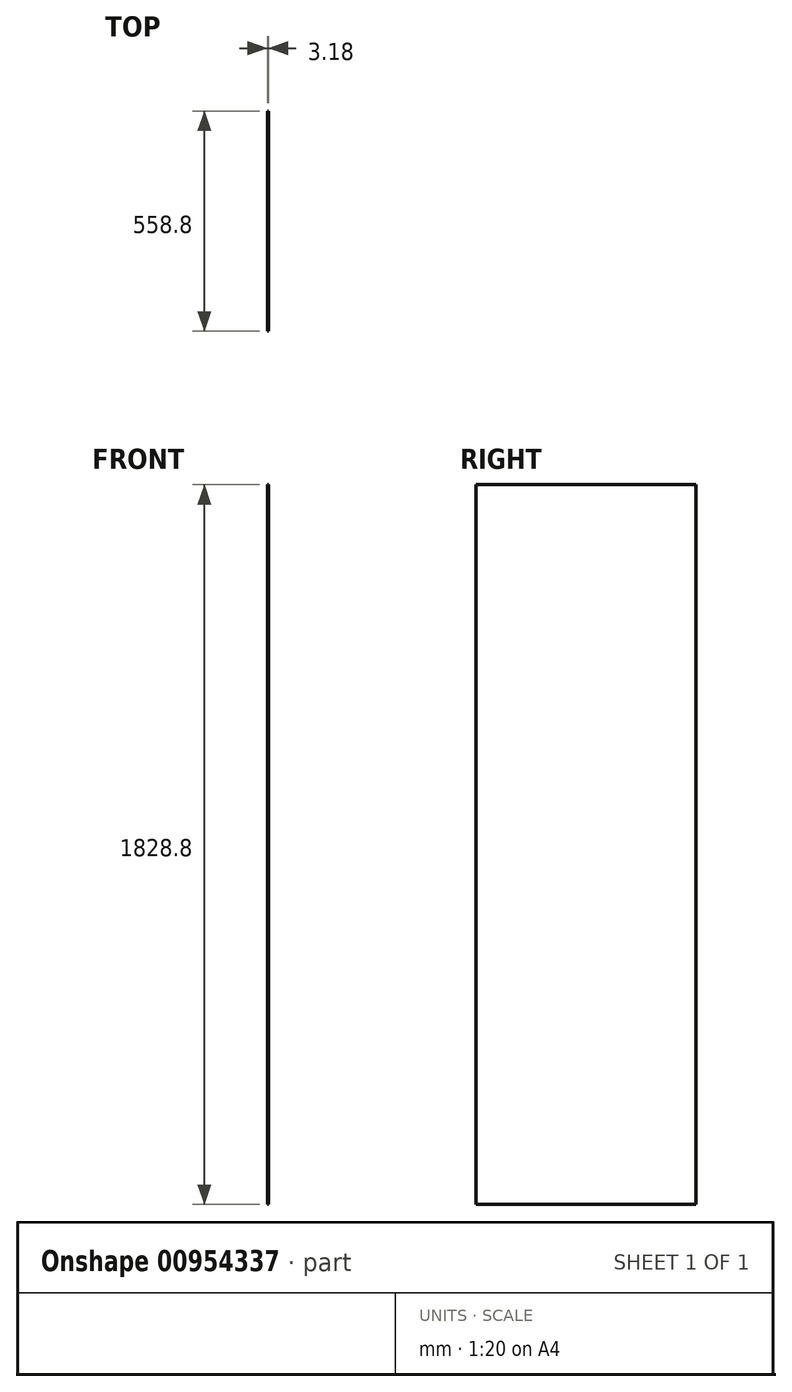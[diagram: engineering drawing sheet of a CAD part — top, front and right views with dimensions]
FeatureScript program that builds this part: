
annotation { "Feature Type Name" : "Feature", "Feature Type Description" : "" }
export const myFeature = defineFeature(function(context is Context, id is Id, definition is map)
    precondition{}
    {
        {
            var Q0;
            Q0=qCreatedBy(makeId("Right.planeOp"),FACE);
            var sketch = newSketch(context, id + "F0", { "sketchPlane" : qUnion([Q0])});
            skLineSegment(sketch, "E0.bottom", {"start": v(266.04, -125.81) * mm, "end": v(-292.76, -125.81) * mm});
            skLineSegment(sketch, "E0.top", {"start": v(266.04, 1702.99) * mm, "end": v(-292.76, 1702.99) * mm});
            skLineSegment(sketch, "E0.left", {"start": v(266.04, -125.81) * mm, "end": v(266.04, 1702.99) * mm});
            skLineSegment(sketch, "E0.right", {"start": v(-292.76, -125.81) * mm, "end": v(-292.76, 1702.99) * mm});
            skPoint(sketch, "E0.middle", {"position": v(-13.36, 788.59) * mm});
            skSolve(sketch);
        }
        {
            var Q0;
            Q0 = qSketchRegion(id + "F0", true);
            extrude(context, id + "F1", {"entities" : qUnion([Q0]), "depth" : 3.17 * mm, "offsetDistance" : 25.4 * mm, "symmetric" : true});
        }
    });
